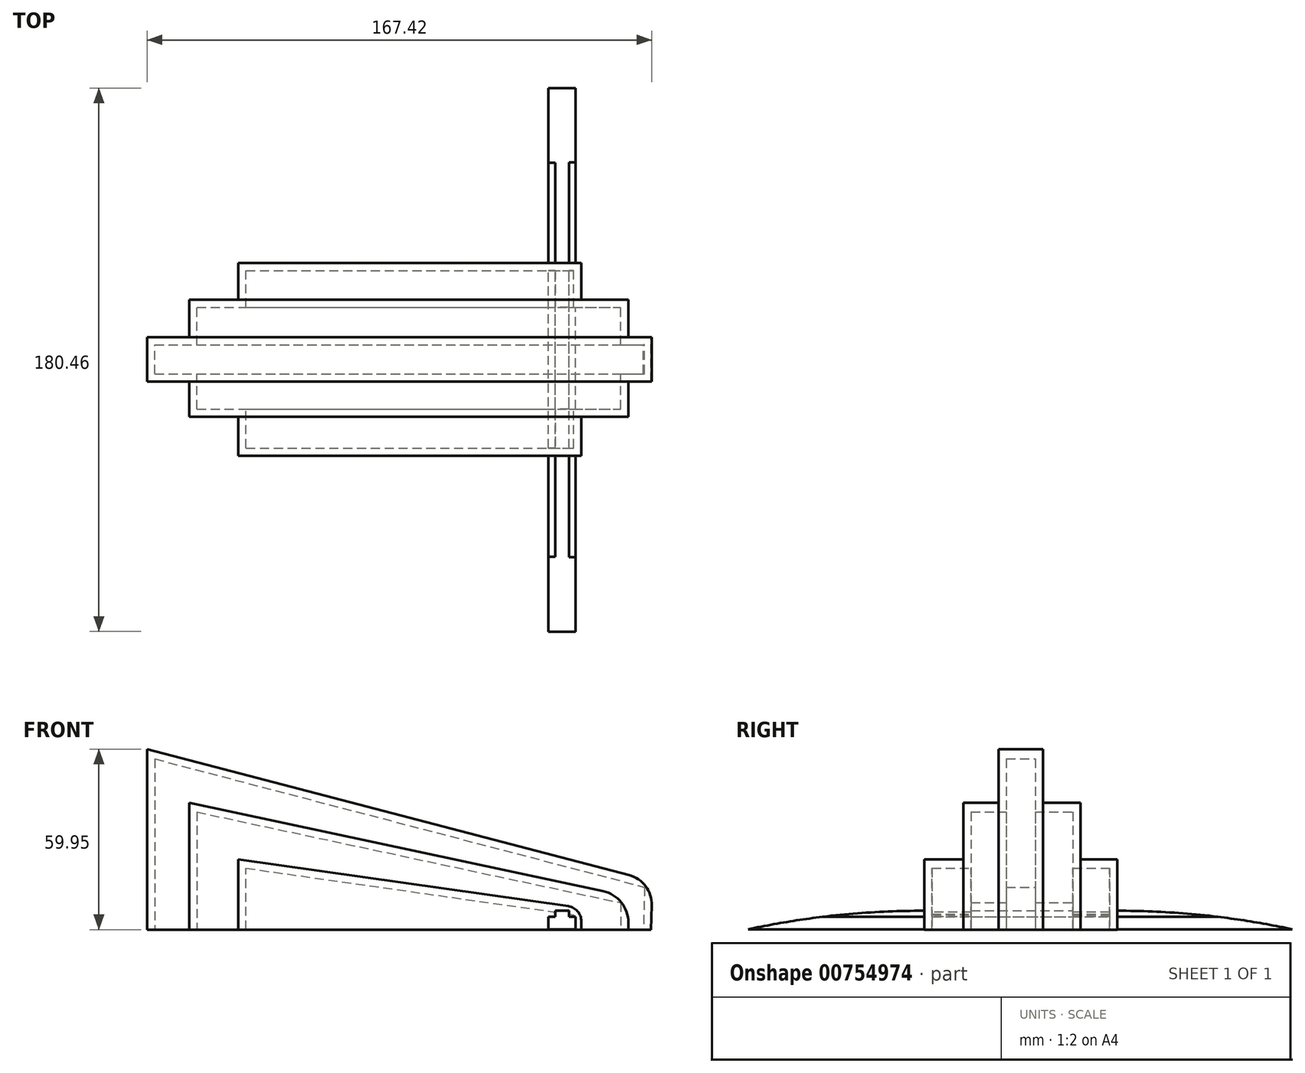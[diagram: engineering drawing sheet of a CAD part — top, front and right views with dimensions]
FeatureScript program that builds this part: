
annotation { "Feature Type Name" : "Feature", "Feature Type Description" : "" }
export const myFeature = defineFeature(function(context is Context, id is Id, definition is map)
    precondition{}
    {
        {
            var Q0;
            Q0=qCreatedBy(makeId("Front.planeOp"),FACE);
            var sketch = newSketch(context, id + "F0", { "sketchPlane" : qUnion([Q0])});
            skLineSegment(sketch, "E0", {"start": v(-27.94, 33.47) * mm, "end": v(-27.94, -26.48) * mm});
            skLineSegment(sketch, "E1", {"start": v(-27.94, 33.47) * mm, "end": v(139.7, -10.43) * mm});
            skLineSegment(sketch, "E2", {"start": v(-28, -26.48) * mm, "end": v(139.24, -26.48) * mm});
            skLineSegment(sketch, "E3", {"start": v(139.7, -10.43) * mm, "end": v(139.24, -26.48) * mm});
            skLineSegment(sketch, "E4", {"start": v(-13.97, 15.7) * mm, "end": v(-13.97, -26.48) * mm});
            skLineSegment(sketch, "E5", {"start": v(-13.97, 15.7) * mm, "end": v(131.72, -15.51) * mm});
            skLineSegment(sketch, "E6", {"start": v(131.72, -15.51) * mm, "end": v(131.72, -26.48) * mm});
            skLineSegment(sketch, "E7", {"start": v(2.36, -26.48) * mm, "end": v(2.36, -3.18) * mm});
            skLineSegment(sketch, "E8", {"start": v(2.36, -3.18) * mm, "end": v(116.11, -19.32) * mm});
            skLineSegment(sketch, "E9", {"start": v(116.11, -19.32) * mm, "end": v(116.11, -26.48) * mm});
            skSolve(sketch);
        }
        {
            var Q0;
            {var subQ0=sQuery(id+"F0.wireOp",EDGE,"E7");Q0=makeQuery(id+"F0.imprint","IMPRINT",FACE,{"disambiguationData":[TD([[makeQuery(id+"F0.imprint","IMPRINT",EDGE,{"derivedFrom":subQ0}),-1.0]])]});}
            extrude(context, id + "F1", {"entities" : qUnion([Q0]), "depth" : 91.7 * mm, "offsetDistance" : 25.4 * mm});
        }
        {
            var Q0;
            {var subQ0=sQuery(id+"F0.wireOp",EDGE,"E4");Q0=makeQuery(id+"F0.imprint","IMPRINT",FACE,{"disambiguationData":[TD([[makeQuery(id+"F0.imprint","IMPRINT",EDGE,{"derivedFrom":subQ0}),1.0]])]});}
            extrude(context, id + "F2", {"entities" : qUnion([Q0]), "operationType" : NewBodyOperationType.ADD, "depth" : 78.74 * mm, "offsetDistance" : 25.4 * mm});
        }
        {
            var Q0;
            {var subQ1=sQuery(id+"F0.wireOp",EDGE,"E0");Q0=makeQuery(id+"F0.imprint","IMPRINT",FACE,{"disambiguationData":[TD([[makeQuery(id+"F0.imprint","IMPRINT",EDGE,{"derivedFrom":subQ1}),1.0]])]});}
            extrude(context, id + "F3", {"entities" : qUnion([Q0]), "operationType" : NewBodyOperationType.ADD, "depth" : 67.06 * mm, "offsetDistance" : 25.4 * mm});
        }
        {
            var Q0;
            {var subQ0=sQuery(id+"F0.wireOp",EDGE,"E7");Q0=makeQuery(id+"F0.imprint","IMPRINT",FACE,{"disambiguationData":[TD([[makeQuery(id+"F0.imprint","IMPRINT",EDGE,{"derivedFrom":subQ0}),-1.0]])]});}
            extrude(context, id + "F4", {"entities" : qUnion([Q0]), "operationType" : NewBodyOperationType.REMOVE, "depth" : 27.7 * mm, "offsetDistance" : 25.4 * mm});
        }
        {
            var Q0;
            {var subQ3=sQuery(id+"F0.wireOp",EDGE,"E4");Q0=makeQuery(id+"F0.imprint","IMPRINT",FACE,{"disambiguationData":[TD([[makeQuery(id+"F0.imprint","IMPRINT",EDGE,{"derivedFrom":subQ3}),1.0]])]});}
            extrude(context, id + "F5", {"entities" : qUnion([Q0]), "operationType" : NewBodyOperationType.REMOVE, "depth" : 39.88 * mm, "offsetDistance" : 25.4 * mm});
        }
        {
            var Q0;
            {var subQ1=sQuery(id+"F0.wireOp",EDGE,"E0");Q0=makeQuery(id+"F0.imprint","IMPRINT",FACE,{"disambiguationData":[TD([[makeQuery(id+"F0.imprint","IMPRINT",EDGE,{"derivedFrom":subQ1}),1.0]])]});}
            extrude(context, id + "F6", {"entities" : qUnion([Q0]), "operationType" : NewBodyOperationType.REMOVE, "depth" : 52.32 * mm, "offsetDistance" : 25.4 * mm});
        }
        {
            var Q0;
            {var subQ0=sQuery(id+"F0.wireOp",EDGE,"E2");var subQ1=makeQuery(id+"F0.imprint","INTERSECT",VERTEX,{"derivedFrom":[subQ0,sQuery(id+"F0.wireOp",EDGE,"E6")]});var subQ2=makeQuery(id+"F0.imprint","INTERSECT",VERTEX,{"derivedFrom":[subQ0,sQuery(id+"F0.wireOp",EDGE,"E4")]});Q0=makeQuery(id+"F3.boolean.opBoolean","MERGE",FACE,{"derivedFrom":[makeQuery(id+"F2.boolean.opBoolean","MERGE",FACE,{"derivedFrom":[makeQuery(id+"F1.opExtrude","SWEPT_FACE",FACE,{"disambiguationData":[OSD([subQ0])]}),makeQuery(id+"F2.opExtrude","SWEPT_FACE",FACE,{"disambiguationData":[OSD([subQ0]),TDD([makeQuery(id+"F0.imprint","IMPRINT",EDGE,{"disambiguationData":[TD([[subQ2,-1.0]])],"derivedFrom":subQ0})])]}),makeQuery(id+"F2.opExtrude","SWEPT_FACE",FACE,{"disambiguationData":[OSD([subQ0]),TDD([makeQuery(id+"F0.imprint","IMPRINT",EDGE,{"disambiguationData":[TD([[subQ1,1.0]])],"derivedFrom":subQ0})])]})]}),makeQuery(id+"F3.opExtrude","SWEPT_FACE",FACE,{"disambiguationData":[OSD([subQ0]),TDD([makeQuery(id+"F0.imprint","IMPRINT",EDGE,{"disambiguationData":[TD([[makeQuery(id+"F0.imprint","INTERSECT",VERTEX,{"derivedFrom":[sQuery(id+"F0.wireOp",EDGE,"E0"),subQ0]}),-1.0]])],"derivedFrom":subQ0})])]}),makeQuery(id+"F3.opExtrude","SWEPT_FACE",FACE,{"disambiguationData":[OSD([subQ0]),TDD([makeQuery(id+"F0.imprint","IMPRINT",EDGE,{"disambiguationData":[TD([[makeQuery(id+"F0.imprint","INTERSECT",VERTEX,{"derivedFrom":[subQ0,sQuery(id+"F0.wireOp",EDGE,"E3")]}),1.0]])],"derivedFrom":subQ0})])]})]});}
            shell(context, id + "F7", {"entities" : qUnion([Q0]), "thickness" : 2.54 * mm});
        }
        {
            var Q0;
            Q0=qCreatedBy(makeId("Front.planeOp"),FACE);
            var sketch = newSketch(context, id + "F8", { "sketchPlane" : qUnion([Q0])});
            skLineSegment(sketch, "E10", {"start": v(105.23, -26.4) * mm, "end": v(105.23, -22.23) * mm});
            skLineSegment(sketch, "E11", {"start": v(105.23, -22.23) * mm, "end": v(107.4, -22.23) * mm});
            skLineSegment(sketch, "E12", {"start": v(107.4, -22.23) * mm, "end": v(107.4, -20.2) * mm});
            skLineSegment(sketch, "E13", {"start": v(107.4, -20.2) * mm, "end": v(111.97, -20.2) * mm});
            skLineSegment(sketch, "E14", {"start": v(111.97, -20.2) * mm, "end": v(111.97, -22.23) * mm});
            skLineSegment(sketch, "E15", {"start": v(111.97, -22.23) * mm, "end": v(114.21, -22.23) * mm});
            skLineSegment(sketch, "E16", {"start": v(114.21, -22.23) * mm, "end": v(114.21, -26.37) * mm});
            skLineSegment(sketch, "E17", {"start": v(114.21, -26.37) * mm, "end": v(105.23, -26.4) * mm});
            skSolve(sketch);
        }
        {
            var Q0;
            Q0=makeQuery(id+"F8.imprint","IMPRINT",FACE,{"disambiguationData":[TD([[makeQuery(id+"F8.imprint","IMPRINT",EDGE,{"derivedFrom":sQuery(id+"F8.wireOp",EDGE,"E10")}),-1.0]])]});
            extrude(context, id + "F9", {"entities" : qUnion([Q0]), "operationType" : NewBodyOperationType.ADD, "depth" : 150.11 * mm, "offsetDistance" : 25.4 * mm});
        }
        {
            var Q0;
            Q0=makeQuery(id+"F9.opExtrude","CAP_FACE",FACE,{"disambiguationData":[OSD([sQuery(id+"F8.wireOp",EDGE,"E10"),sQuery(id+"F8.wireOp",EDGE,"E11"),sQuery(id+"F8.wireOp",EDGE,"E12"),sQuery(id+"F8.wireOp",EDGE,"E13"),sQuery(id+"F8.wireOp",EDGE,"E14"),sQuery(id+"F8.wireOp",EDGE,"E15"),sQuery(id+"F8.wireOp",EDGE,"E16"),sQuery(id+"F8.wireOp",EDGE,"E17")])],"isStart":true});
            extrude(context, id + "F10", {"entities" : qUnion([Q0]), "operationType" : NewBodyOperationType.ADD, "depth" : 30.35 * mm, "offsetDistance" : 25.4 * mm});
        }
        {
            var Q0;
            Q0=makeQuery(id+"F9.opExtrude","CAP_EDGE",EDGE,{"disambiguationData":[OSD([sQuery(id+"F8.wireOp",EDGE,"E13")])],"isStart":false});
            fillet(context, id + "F11", {"entities" : qUnion([Q0]), "radius" : 275.94 * mm, "tangentPropagation" : true, "allowEdgeOverflow" : false});
        }
        {
            var Q0;
            Q0=makeQuery(id+"F10.opExtrude","CAP_EDGE",EDGE,{"disambiguationData":[OSD([sQuery(id+"F8.wireOp",EDGE,"E13")])],"isStart":false});
            fillet(context, id + "F12", {"entities" : qUnion([Q0]), "radius" : 275.95 * mm, "tangentPropagation" : true, "allowEdgeOverflow" : false});
        }
        {
            var Q0;
            Q0=makeQuery(id+"F3.opExtrude","SWEPT_EDGE",EDGE,{"disambiguationData":[OSD([sQuery(id+"F0.wireOp",EDGE,"E1"),sQuery(id+"F0.wireOp",EDGE,"E3")])]});
            fillet(context, id + "F13", {"entities" : qUnion([Q0]), "radius" : 10.07 * mm, "tangentPropagation" : true, "allowEdgeOverflow" : false});
        }
        {
            var Q0;
            Q0=makeQuery(id+"F2.opExtrude","SWEPT_EDGE",EDGE,{"disambiguationData":[OSD([sQuery(id+"F0.wireOp",EDGE,"E5"),sQuery(id+"F0.wireOp",EDGE,"E6")])]});
            fillet(context, id + "F14", {"entities" : qUnion([Q0]), "radius" : 10.66 * mm, "tangentPropagation" : true, "allowEdgeOverflow" : false});
        }
        {
            var Q0;
            Q0=makeQuery(id+"F1.opExtrude","SWEPT_EDGE",EDGE,{"disambiguationData":[OSD([sQuery(id+"F0.wireOp",EDGE,"E8"),sQuery(id+"F0.wireOp",EDGE,"E9")])]});
            fillet(context, id + "F15", {"entities" : qUnion([Q0]), "radius" : 5.08 * mm, "tangentPropagation" : true, "allowEdgeOverflow" : false});
        }
        {
            var Q0;
            Q0=makeQuery(id+"F6.boolean.opBoolean","COPY",EDGE,{"derivedFrom":makeQuery(id+"F6.opExtrude","SWEPT_EDGE",EDGE,{"disambiguationData":[OSD([sQuery(id+"F0.wireOp",EDGE,"E5"),sQuery(id+"F0.wireOp",EDGE,"E6")])]})});
            fillet(context, id + "F16", {"entities" : qUnion([Q0]), "radius" : 10.67 * mm, "tangentPropagation" : true, "allowEdgeOverflow" : false});
        }
        {
            var Q0;
            Q0=makeQuery(id+"F5.boolean.opBoolean","COPY",EDGE,{"derivedFrom":makeQuery(id+"F5.opExtrude","SWEPT_EDGE",EDGE,{"disambiguationData":[OSD([sQuery(id+"F0.wireOp",EDGE,"E8"),sQuery(id+"F0.wireOp",EDGE,"E9")])]})});
            fillet(context, id + "F17", {"entities" : qUnion([Q0]), "radius" : 5.08 * mm, "tangentPropagation" : true, "allowEdgeOverflow" : false});
        }
    });
